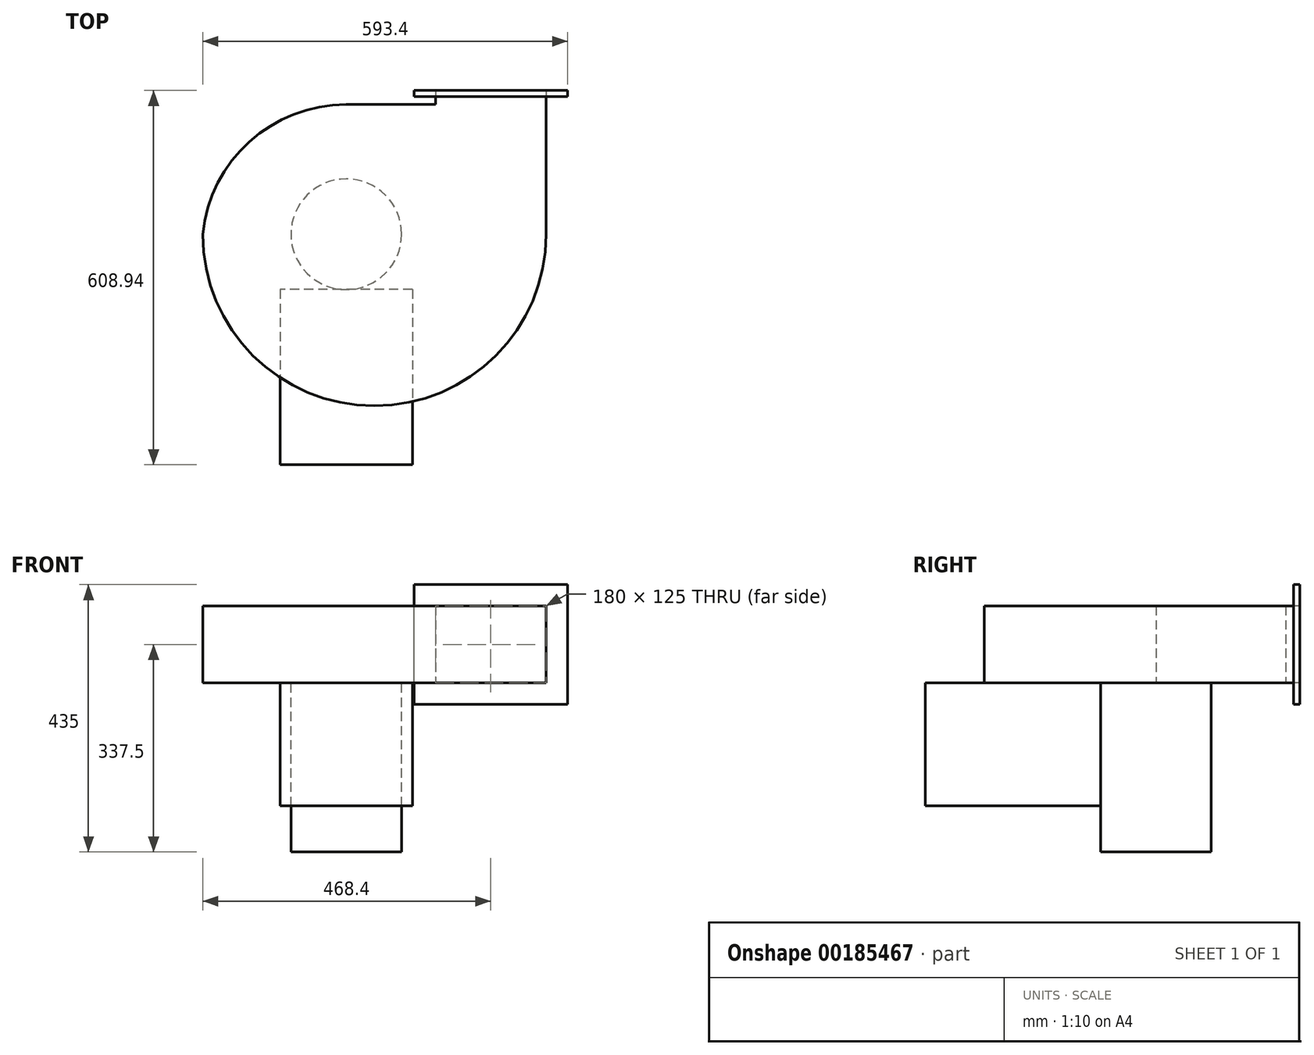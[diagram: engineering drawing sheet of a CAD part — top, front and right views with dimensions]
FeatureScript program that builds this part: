
annotation { "Feature Type Name" : "Feature", "Feature Type Description" : "" }
export const myFeature = defineFeature(function(context is Context, id is Id, definition is map)
    precondition{}
    {
        {
            var Q0;
            Q0=qCreatedBy(makeId("Top.planeOp"),FACE);
            var sketch = newSketch(context, id + "F0", { "sketchPlane" : qUnion([Q0])});
            skCircle(sketch, "E0", {"center": v(0, 0) * mm, "radius": 44.99 * mm});
            skCircle(sketch, "E1", {"center": v(0, 0) * mm, "radius": 78.48 * mm});
            skCircle(sketch, "E2", {"center": v(0, 0) * mm, "radius": 133.47 * mm});
            skCircle(sketch, "E3", {"center": v(0, 0) * mm, "radius": 192.49 * mm});
            skLineSegment(sketch, "E4", {"start": v(-351.57, 0) * mm, "end": v(350.43, 0) * mm, "construction": true});
            skLineSegment(sketch, "E5", {"start": v(0, 261.68) * mm, "end": v(0, -346.42) * mm, "construction": true});
            skLineSegment(sketch, "E6", {"start": v(325, 0) * mm, "end": v(325, 223.94) * mm});
            skLineSegment(sketch, "E7", {"start": v(325, 223.94) * mm, "end": v(145, 223.94) * mm});
            skLineSegment(sketch, "E8", {"start": v(145, 223.94) * mm, "end": v(145, 211.17) * mm});
            skLineSegment(sketch, "E9", {"start": v(145, 211.17) * mm, "end": v(0, 211.17) * mm});
            skArc(sketch, "E10", {"start": v(0, 211.17) * mm, "mid": v(-157.38, 150.54) * mm, "end": v(-233.4, 0) * mm});
            skLineSegment(sketch, "E11", {"start": v(235, 197.25) * mm, "end": v(235, 290.95) * mm, "construction": true});
            skLineSegment(sketch, "E12.top", {"start": v(411.6, 280) * mm, "end": v(58.4, 280) * mm});
            skLineSegment(sketch, "E12.left", {"start": v(411.6, 223.94) * mm, "end": v(411.6, 280) * mm});
            skLineSegment(sketch, "E12.right", {"start": v(58.4, 223.94) * mm, "end": v(58.4, 280) * mm});
            skPoint(sketch, "E12.middle", {"position": v(235, 251.97) * mm});
            skArc(sketch, "E13", {"start": v(325, 0) * mm, "mid": v(45.8, -279.2) * mm, "end": v(-233.4, 0) * mm});
            skSolve(sketch);
        }
        {
            var Q0;
            Q0=makeQuery(id+"F0.imprint","IMPRINT",FACE,{"disambiguationData":[TD([[makeQuery(id+"F0.imprint","IMPRINT",EDGE,{"derivedFrom":sQuery(id+"F0.wireOp",EDGE,"E3")}),-1.0]])]});
            var Q1;
            Q1=makeQuery(id+"F0.imprint","IMPRINT",FACE,{"disambiguationData":[TD([[makeQuery(id+"F0.imprint","IMPRINT",EDGE,{"derivedFrom":sQuery(id+"F0.wireOp",EDGE,"E2")}),-1.0]])]});
            var Q2;
            Q2=makeQuery(id+"F0.imprint","IMPRINT",FACE,{"disambiguationData":[TD([[makeQuery(id+"F0.imprint","IMPRINT",EDGE,{"derivedFrom":sQuery(id+"F0.wireOp",EDGE,"E0")}),-1.0]])]});
            var Q3;
            Q3=makeQuery(id+"F0.imprint","IMPRINT",FACE,{"disambiguationData":[TD([[makeQuery(id+"F0.imprint","IMPRINT",EDGE,{"derivedFrom":sQuery(id+"F0.wireOp",EDGE,"E1")}),-1.0]])]});
            var Q4;
            Q4=makeQuery(id+"F0.imprint","IMPRINT",FACE,{"disambiguationData":[TD([[makeQuery(id+"F0.imprint","IMPRINT",EDGE,{"derivedFrom":sQuery(id+"F0.wireOp",EDGE,"E0")}),1.0]])]});
            extrude(context, id + "F1", {"entities" : qUnion([Q0, Q1, Q2, Q3, Q4]), "depth" : 125 * mm});
        }
        {
            var Q0;
            Q0=makeQuery(id+"F1.opExtrude","SWEPT_FACE",FACE,{"disambiguationData":[OSD([sQuery(id+"F0.wireOp",EDGE,"E7")])]});
            var sketch = newSketch(context, id + "F2", { "sketchPlane" : qUnion([Q0])});
            skLineSegment(sketch, "E14.bottom", {"start": v(-110, -35) * mm, "end": v(-360, -35) * mm});
            skLineSegment(sketch, "E14.top", {"start": v(-110, 160) * mm, "end": v(-360, 160) * mm});
            skLineSegment(sketch, "E14.left", {"start": v(-110, -35) * mm, "end": v(-110, 160) * mm});
            skLineSegment(sketch, "E14.right", {"start": v(-360, -35) * mm, "end": v(-360, 160) * mm});
            skPoint(sketch, "E14.middle", {"position": v(-235, 62.5) * mm});
            skLineSegment(sketch, "E15.bottom", {"start": v(-145, 0) * mm, "end": v(-325, 0) * mm});
            skLineSegment(sketch, "E15.top", {"start": v(-145, 125) * mm, "end": v(-325, 125) * mm});
            skLineSegment(sketch, "E15.left", {"start": v(-145, 0) * mm, "end": v(-145, 125) * mm});
            skLineSegment(sketch, "E15.right", {"start": v(-325, 0) * mm, "end": v(-325, 125) * mm});
            skSolve(sketch);
        }
        {
            var Q0;
            Q0 = qSketchRegion(id + "F2", true);
            extrude(context, id + "F3", {"entities" : qUnion([Q0]), "depth" : 10 * mm});
        }
        {
            var Q0;
            Q0=makeQuery(id+"F1.opExtrude","CAP_FACE",FACE,{"disambiguationData":[OSD([sQuery(id+"F0.wireOp",EDGE,"E6"),sQuery(id+"F0.wireOp",EDGE,"E7"),sQuery(id+"F0.wireOp",EDGE,"E8"),sQuery(id+"F0.wireOp",EDGE,"E9"),sQuery(id+"F0.wireOp",EDGE,"E10"),sQuery(id+"F0.wireOp",EDGE,"E13")])],"isStart":true});
            var sketch = newSketch(context, id + "F4", { "sketchPlane" : qUnion([Q0])});
            skLineSegment(sketch, "E16", {"start": v(0, 0) * mm, "end": v(428.59, 0) * mm, "construction": true});
            skLineSegment(sketch, "E17", {"start": v(0, 0) * mm, "end": v(0, 275.42) * mm, "construction": true});
            skCircle(sketch, "E18", {"center": v(0, 0) * mm, "radius": 90 * mm});
            skSolve(sketch);
        }
        {
            var Q0;
            Q0=makeQuery(id+"F4.imprint","IMPRINT",FACE,{"disambiguationData":[TD([[makeQuery(id+"F4.imprint","IMPRINT",EDGE,{"derivedFrom":sQuery(id+"F4.wireOp",EDGE,"E18")}),1.0]])]});
            extrude(context, id + "F5", {"entities" : qUnion([Q0]), "operationType" : NewBodyOperationType.ADD, "depth" : 275 * mm});
        }
        {
            var Q0;
            Q0=makeQuery(id+"F1.opExtrude","CAP_FACE",FACE,{"disambiguationData":[OSD([sQuery(id+"F0.wireOp",EDGE,"E6"),sQuery(id+"F0.wireOp",EDGE,"E7"),sQuery(id+"F0.wireOp",EDGE,"E8"),sQuery(id+"F0.wireOp",EDGE,"E9"),sQuery(id+"F0.wireOp",EDGE,"E10"),sQuery(id+"F0.wireOp",EDGE,"E13")])],"isStart":true});
            var sketch = newSketch(context, id + "F6", { "sketchPlane" : qUnion([Q0])});
            skLineSegment(sketch, "E19.bottom", {"start": v(107.5, 90) * mm, "end": v(-107.5, 90) * mm});
            skLineSegment(sketch, "E19.top", {"start": v(107.5, 375) * mm, "end": v(-107.5, 375) * mm});
            skLineSegment(sketch, "E19.left", {"start": v(107.5, 90) * mm, "end": v(107.5, 375) * mm});
            skLineSegment(sketch, "E19.right", {"start": v(-107.5, 90) * mm, "end": v(-107.5, 375) * mm});
            skPoint(sketch, "E19.middle", {"position": v(0, 232.5) * mm});
            skSolve(sketch);
        }
        {
            var Q0;
            Q0 = qSketchRegion(id + "F6", true);
            extrude(context, id + "F7", {"entities" : qUnion([Q0]), "depth" : 200 * mm});
        }
    });
